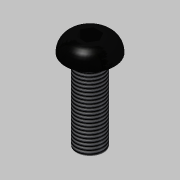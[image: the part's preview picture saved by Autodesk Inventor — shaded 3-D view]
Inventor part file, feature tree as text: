
AUTODESK INVENTOR PART (.ipt)
format: ipt  version: 2014 (Build 180170000, 170)  size: 116,736 bytes
history: native  units: mm
features: extrude x3, sketch x3, fillet x1, thread x1, reference x1
ambient origin geometry x8: Origin, YZ Plane, XZ Plane, XY Plane, X Axis, Y Axis, Z Axis, Center Point
bodies: Solid1 (feature_tree)
feature tree (9):
  extrude  "Extrusion1"  Depth=12.0mm TaperAngle=0.0deg
  extrude  "Extrusion2"  Depth=2.3mm TaperAngle=0.0deg
  fillet  "Fillet1"  Radius=2.2mm
  extrude  "Extrusion4"  Depth=10.0mm TaperAngle=0.0deg
  thread  "Thread1"  [1 undecoded]
  sketch  "Sketch1"  dims[d0=4.0mm d1=12.0mm d2=0.0mm]
  reference  "Reference1"
  sketch  "Sketch2"  dims[d3=7.3mm d4=2.3mm d5=0.0mm d6=2.2mm]
  sketch  "Sketch4"  dims[d10=2.5mm d11=4.0mm d12=0.0mm d13=10.0mm d14=0.0mm]
note: 1 required parameter value undecoded (feature->parameter linkage not recoverable at this tier; creation-order binding heuristic only, values carry confidence <= 0.55)
